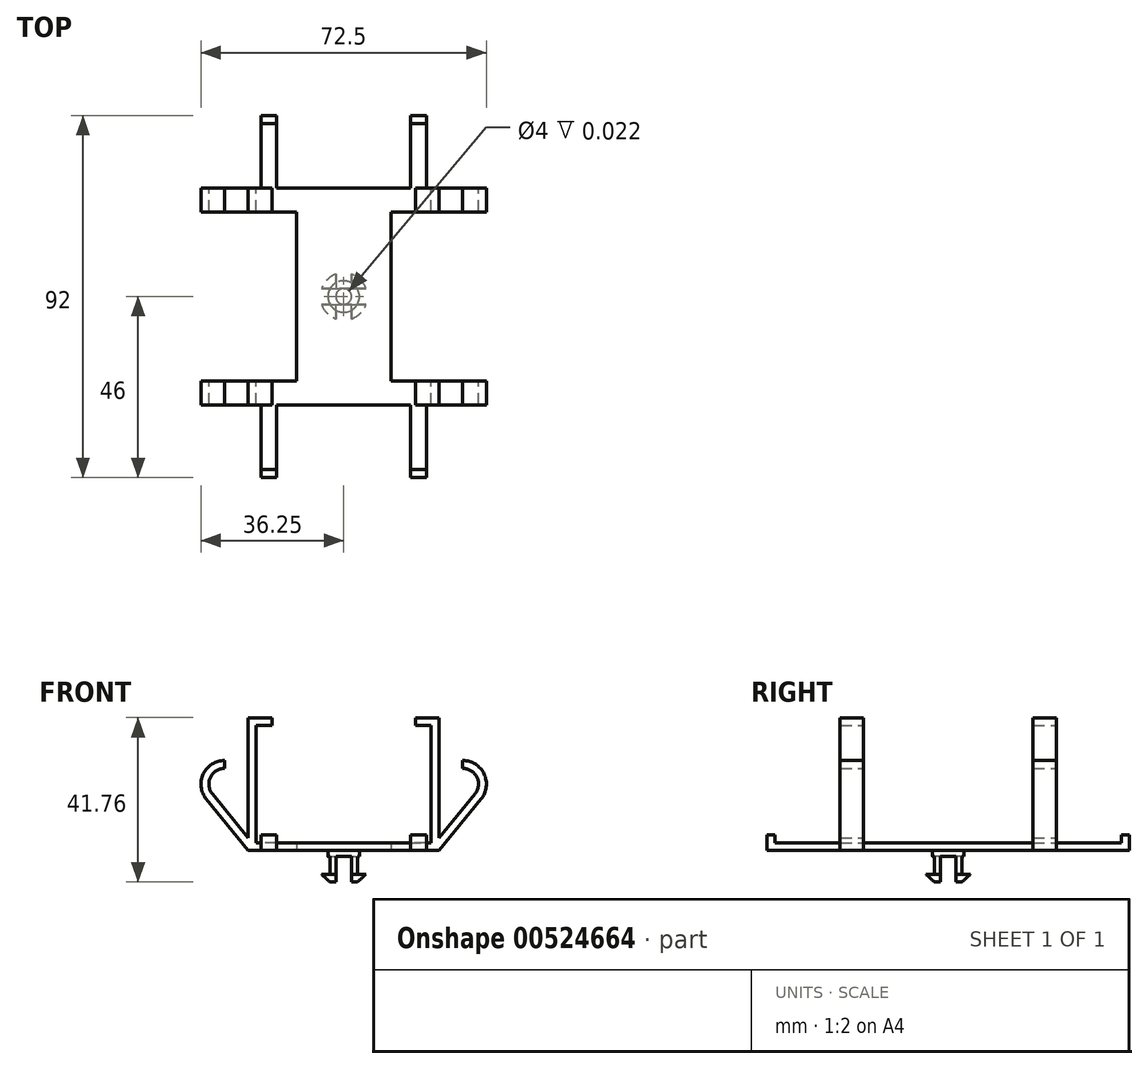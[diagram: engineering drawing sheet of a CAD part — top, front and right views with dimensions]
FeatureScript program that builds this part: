
annotation { "Feature Type Name" : "Feature", "Feature Type Description" : "" }
export const myFeature = defineFeature(function(context is Context, id is Id, definition is map)
    precondition{}
    {
        {
            var Q0;
            Q0=qCreatedBy(makeId("Front.planeOp"),FACE);
            var sketch = newSketch(context, id + "F0", { "sketchPlane" : qUnion([Q0])});
            skLineSegment(sketch, "E0.bottom", {"start": v(-22.25, 14.88) * mm, "end": v(22.25, 14.88) * mm});
            skLineSegment(sketch, "E0.top", {"start": v(-22.25, -14.88) * mm, "end": v(22.25, -14.88) * mm});
            skLineSegment(sketch, "E0.left", {"start": v(-22.25, 14.88) * mm, "end": v(-22.25, -14.88) * mm});
            skLineSegment(sketch, "E0.right", {"start": v(22.25, 14.88) * mm, "end": v(22.25, -14.88) * mm});
            skPoint(sketch, "E0.middle", {"position": v(0, 0) * mm});
            skLineSegment(sketch, "E1.bottom", {"start": v(24.25, 16.88) * mm, "end": v(18.25, 16.88) * mm});
            skLineSegment(sketch, "E1.top", {"start": v(24.25, -16.88) * mm, "end": v(4, -16.88) * mm});
            skLineSegment(sketch, "E1.left", {"start": v(24.25, 16.88) * mm, "end": v(24.25, -16.88) * mm});
            skLineSegment(sketch, "E1.right", {"start": v(-24.25, 16.88) * mm, "end": v(-24.25, -16.88) * mm});
            skLineSegment(sketch, "E2", {"start": v(-18.25, 16.88) * mm, "end": v(-18.25, 14.88) * mm});
            skLineSegment(sketch, "E3", {"start": v(18.25, 16.88) * mm, "end": v(18.25, 14.88) * mm});
            skLineSegment(sketch, "E4.trimOffspring", {"start": v(-18.25, 16.88) * mm, "end": v(-24.25, 16.88) * mm});
            skLineSegment(sketch, "E5.top", {"start": v(2, -24.88) * mm, "end": v(4, -24.88) * mm});
            skLineSegment(sketch, "E5.left", {"start": v(2, -18.35) * mm, "end": v(2, -24.88) * mm});
            skLineSegment(sketch, "E5.right", {"start": v(4, -16.88) * mm, "end": v(4, -22.88) * mm});
            skLineSegment(sketch, "E6", {"start": v(4, -24.88) * mm, "end": v(6, -22.88) * mm});
            skLineSegment(sketch, "E7", {"start": v(6, -22.88) * mm, "end": v(4, -22.88) * mm});
            skLineSegment(sketch, "E8.trimOffspring", {"start": v(2, -16.88) * mm, "end": v(-24.25, -16.87) * mm});
            skLineSegment(sketch, "E9", {"start": v(4, -16.88) * mm, "end": v(2, -16.88) * mm});
            skLineSegment(sketch, "E10", {"start": v(2, -18.35) * mm, "end": v(0, -18.35) * mm});
            skLineSegment(sketch, "E11", {"start": v(0, -18.35) * mm, "end": v(0, -16.88) * mm});
            skSolve(sketch);
        }
        {
            var Q0;
            Q0=makeQuery(id+"F0.imprint","IMPRINT",FACE,{"disambiguationData":[TD([[makeQuery(id+"F0.imprint","IMPRINT",EDGE,{"derivedFrom":sQuery(id+"F0.wireOp",EDGE,"E5.top")}),1.0]])]});
            var Q1;
            Q1=sQuery(id+"F0.wireOp",EDGE,"E11");
            revolve(context, id + "F1", {"entities" : qUnion([Q0]), "axis" : qUnion([Q1]), "revolveType" : RevolveType.FULL});
        }
        {
            var Q0;
            Q0=qCreatedBy(makeId("Front.planeOp"),FACE);
            var sketch = newSketch(context, id + "F2", { "sketchPlane" : qUnion([Q0])});
            skArc(sketch, "E12", {"start": v(33.35, -2.53) * mm, "mid": v(33.86, 1.72) * mm, "end": v(30.25, 4) * mm});
            skArc(sketch, "E13", {"start": v(34.9, -3.79) * mm, "mid": v(35.67, 2.58) * mm, "end": v(30.25, 6) * mm});
            skLineSegment(sketch, "E14", {"start": v(34.9, -3.79) * mm, "end": v(24.25, -16.88) * mm});
            skLineSegment(sketch, "E15", {"start": v(24.25, -16.88) * mm, "end": v(24.25, -13.7) * mm});
            skLineSegment(sketch, "E16.0", {"start": v(33.35, -2.53) * mm, "end": v(24.25, -13.7) * mm});
            skLineSegment(sketch, "E17", {"start": v(30.25, 4) * mm, "end": v(30.25, 6) * mm});
            skArc(sketch, "E18.MirrorCS", {"start": v(-34.9, -3.79) * mm, "mid": v(-35.67, 2.58) * mm, "end": v(-30.25, 6) * mm});
            skLineSegment(sketch, "E19.MirrorCS", {"start": v(-33.35, -2.53) * mm, "end": v(-24.25, -13.7) * mm});
            skArc(sketch, "E20.MirrorCS", {"start": v(-33.35, -2.53) * mm, "mid": v(-33.86, 1.72) * mm, "end": v(-30.25, 4) * mm});
            skLineSegment(sketch, "E21.MirrorCS", {"start": v(-30.25, 4) * mm, "end": v(-30.25, 6) * mm});
            skLineSegment(sketch, "E22.MirrorCS", {"start": v(-24.25, -16.88) * mm, "end": v(-24.25, -13.7) * mm});
            skLineSegment(sketch, "E23.MirrorCS", {"start": v(-34.9, -3.79) * mm, "end": v(-24.25, -16.88) * mm});
            skSolve(sketch);
        }
        {
            var Q0;
            Q0=makeQuery(id+"F0.imprint","IMPRINT",FACE,{"disambiguationData":[TD([[makeQuery(id+"F0.imprint","IMPRINT",EDGE,{"derivedFrom":sQuery(id+"F0.wireOp",EDGE,"E0.top")}),-1.0]])]});
            extrude(context, id + "F3", {"entities" : qUnion([Q0]), "operationType" : NewBodyOperationType.ADD, "endBound" : BoundingType.SYMMETRIC, "depth" : 55 * mm, "offsetDistance" : 25 * mm});
        }
        {
            var Q0;
            Q0=makeQuery(id+"F3.opExtrude","SWEPT_FACE",FACE,{"disambiguationData":[OSD([sQuery(id+"F0.wireOp",EDGE,"E1.top"),sQuery(id+"F0.wireOp",EDGE,"E8.trimOffspring"),sQuery(id+"F0.wireOp",EDGE,"E9")])]});
            var sketch = newSketch(context, id + "F4", { "sketchPlane" : qUnion([Q0])});
            skPoint(sketch, "E24.start.orphan", {"position": v(-24.25, 20) * mm});
            skPoint(sketch, "E25.end.orphan", {"position": v(-18.25, 0) * mm});
            skPoint(sketch, "E25.start.orphan", {"position": v(-18.25, 20) * mm});
            skPoint(sketch, "E26.MirrorCS.end.orphan", {"position": v(-18.25, -20) * mm});
            skPoint(sketch, "E26.MirrorCS.start.orphan", {"position": v(-24.25, -20) * mm});
            skPoint(sketch, "E27.MirrorCS.start.orphan", {"position": v(24.25, 20) * mm});
            skPoint(sketch, "E28.MirrorCS.end.orphan", {"position": v(18.25, 0) * mm});
            skPoint(sketch, "E28.MirrorCS.start.orphan", {"position": v(18.25, 20) * mm});
            skPoint(sketch, "E29.MirrorCS.end.orphan", {"position": v(18.25, -20) * mm});
            skPoint(sketch, "E29.MirrorCS.start.orphan", {"position": v(24.25, -20) * mm});
            skLineSegment(sketch, "E30.bottom", {"start": v(-40, 21.5) * mm, "end": v(-12, 21.5) * mm});
            skLineSegment(sketch, "E30.top", {"start": v(-40, -21.5) * mm, "end": v(-12, -21.5) * mm});
            skLineSegment(sketch, "E30.left", {"start": v(-40, 21.5) * mm, "end": v(-40, -21.5) * mm});
            skLineSegment(sketch, "E30.right", {"start": v(-12, 21.5) * mm, "end": v(-12, -21.5) * mm});
            skPoint(sketch, "E30.middle", {"position": v(-26, 0) * mm});
            skLineSegment(sketch, "E31.MirrorCS", {"start": v(40, -21.5) * mm, "end": v(12, -21.5) * mm});
            skLineSegment(sketch, "E32.MirrorCS", {"start": v(40, 21.5) * mm, "end": v(40, -21.5) * mm});
            skPoint(sketch, "E33.MirrorP", {"position": v(26, 0) * mm});
            skLineSegment(sketch, "E34.MirrorCS", {"start": v(12, 21.5) * mm, "end": v(12, -21.5) * mm});
            skLineSegment(sketch, "E35.MirrorCS", {"start": v(40, 21.5) * mm, "end": v(12, 21.5) * mm});
            skSolve(sketch);
        }
        {
            var Q0;
            Q0 = qSketchRegion(id + "F2", true);
            extrude(context, id + "F5", {"entities" : qUnion([Q0]), "operationType" : NewBodyOperationType.ADD, "endBound" : BoundingType.SYMMETRIC, "depth" : 55 * mm, "offsetDistance" : 25 * mm});
        }
        {
            var Q0;
            {var subQ0=sQuery(id+"F4.wireOp",EDGE,"E30.left");Q0=makeQuery(id+"F4.imprint","IMPRINT",FACE,{"disambiguationData":[TD([[makeQuery(id+"F4.imprint","IMPRINT",EDGE,{"derivedFrom":subQ0}),1.0]])]});}
            var Q1;
            {var subQ0=sQuery(id+"F4.wireOp",EDGE,"E30.right");Q1=makeQuery(id+"F4.imprint","IMPRINT",FACE,{"disambiguationData":[TD([[makeQuery(id+"F4.imprint","IMPRINT",EDGE,{"derivedFrom":subQ0}),-1.0]])]});}
            var Q2;
            {var subQ0=sQuery(id+"F4.wireOp",EDGE,"E34.MirrorCS");Q2=makeQuery(id+"F4.imprint","IMPRINT",FACE,{"disambiguationData":[TD([[makeQuery(id+"F4.imprint","IMPRINT",EDGE,{"derivedFrom":subQ0}),1.0]])]});}
            var Q3;
            {var subQ0=sQuery(id+"F4.wireOp",EDGE,"E32.MirrorCS");Q3=makeQuery(id+"F4.imprint","IMPRINT",FACE,{"disambiguationData":[TD([[makeQuery(id+"F4.imprint","IMPRINT",EDGE,{"derivedFrom":subQ0}),-1.0]])]});}
            extrude(context, id + "F6", {"entities" : qUnion([Q0, Q1, Q2, Q3]), "operationType" : NewBodyOperationType.REMOVE, "endBound" : BoundingType.THROUGH_ALL, "oppositeDirection" : true, "depth" : 25 * mm, "offsetDistance" : 25 * mm});
        }
        {
            var Q0;
            Q0=qCreatedBy(makeId("Right.planeOp"),FACE);
            var sketch = newSketch(context, id + "F7", { "sketchPlane" : qUnion([Q0])});
            skLineSegment(sketch, "E36", {"start": v(-27.5, -16.88) * mm, "end": v(-46, -16.88) * mm});
            skLineSegment(sketch, "E37", {"start": v(-46, -16.88) * mm, "end": v(-46, -12.88) * mm});
            skLineSegment(sketch, "E38", {"start": v(-46, -12.88) * mm, "end": v(-44, -12.88) * mm});
            skLineSegment(sketch, "E39", {"start": v(-44, -12.88) * mm, "end": v(-44, -14.88) * mm});
            skLineSegment(sketch, "E40", {"start": v(-44, -14.88) * mm, "end": v(-27.5, -14.88) * mm});
            skLineSegment(sketch, "E41.MirrorCS", {"start": v(46, -12.88) * mm, "end": v(44, -12.88) * mm});
            skLineSegment(sketch, "E42.MirrorCS", {"start": v(44, -12.88) * mm, "end": v(44, -14.88) * mm});
            skLineSegment(sketch, "E43.MirrorCS", {"start": v(27.5, -16.88) * mm, "end": v(46, -16.88) * mm});
            skLineSegment(sketch, "E44.MirrorCS", {"start": v(46, -16.88) * mm, "end": v(46, -12.88) * mm});
            skLineSegment(sketch, "E45.MirrorCS", {"start": v(44, -14.88) * mm, "end": v(27.5, -14.88) * mm});
            skLineSegment(sketch, "E46", {"start": v(-27.5, -14.87) * mm, "end": v(-27.5, -16.88) * mm});
            skLineSegment(sketch, "E47", {"start": v(27.5, -14.87) * mm, "end": v(27.5, -16.88) * mm});
            skSolve(sketch);
        }
        {
            var Q0;
            Q0 = qSketchRegion(id + "F7", true);
            extrude(context, id + "F8", {"entities" : qUnion([Q0]), "operationType" : NewBodyOperationType.ADD, "endBound" : BoundingType.SYMMETRIC, "depth" : 42 * mm, "offsetDistance" : 25 * mm});
        }
        {
            var Q0;
            Q0=makeQuery(id+"F8.boolean.opBoolean","MERGE",FACE,{"derivedFrom":[makeQuery(id+"F3.opExtrude","SWEPT_FACE",FACE,{"disambiguationData":[OSD([sQuery(id+"F0.wireOp",EDGE,"E1.top"),sQuery(id+"F0.wireOp",EDGE,"E8.trimOffspring"),sQuery(id+"F0.wireOp",EDGE,"E9")])]}),makeQuery(id+"F8.opExtrude","SWEPT_FACE",FACE,{"disambiguationData":[OSD([sQuery(id+"F7.wireOp",EDGE,"E36")])]}),makeQuery(id+"F8.opExtrude","SWEPT_FACE",FACE,{"disambiguationData":[OSD([sQuery(id+"F7.wireOp",EDGE,"E43.MirrorCS")])]})]});
            var sketch = newSketch(context, id + "F9", { "sketchPlane" : qUnion([Q0])});
            skLineSegment(sketch, "E48", {"start": v(-17, 46) * mm, "end": v(-17, 27.5) * mm});
            skLineSegment(sketch, "E49", {"start": v(-17, 27.5) * mm, "end": v(0, 27.5) * mm});
            skPoint(sketch, "E50.orphan", {"position": v(-17, 20) * mm});
            skLineSegment(sketch, "E51.MirrorCS", {"start": v(17, 46) * mm, "end": v(17, 27.5) * mm});
            skLineSegment(sketch, "E52.MirrorCS", {"start": v(17, 27.5) * mm, "end": v(0, 27.5) * mm});
            skLineSegment(sketch, "E53.MirrorCS", {"start": v(17, -46) * mm, "end": v(17, -27.5) * mm});
            skLineSegment(sketch, "E54.MirrorCS", {"start": v(-17, -46) * mm, "end": v(-17, -27.5) * mm});
            skLineSegment(sketch, "E55.MirrorCS", {"start": v(17, -27.5) * mm, "end": v(0, -27.5) * mm});
            skLineSegment(sketch, "E56.MirrorCS", {"start": v(-17, -27.5) * mm, "end": v(0, -27.5) * mm});
            skSolve(sketch);
        }
        {
            var Q0;
            {var subQ1=sQuery(id+"F9.wireOp",EDGE,"E48");Q0=makeQuery(id+"F9.imprint","IMPRINT",FACE,{"disambiguationData":[TD([[makeQuery(id+"F9.imprint","IMPRINT",EDGE,{"derivedFrom":subQ1}),1.0]])]});}
            var Q1;
            {var subQ1=sQuery(id+"F9.wireOp",EDGE,"E54.MirrorCS");Q1=makeQuery(id+"F9.imprint","IMPRINT",FACE,{"disambiguationData":[TD([[makeQuery(id+"F9.imprint","IMPRINT",EDGE,{"derivedFrom":subQ1}),-1.0]])]});}
            extrude(context, id + "F10", {"entities" : qUnion([Q0, Q1]), "operationType" : NewBodyOperationType.REMOVE, "endBound" : BoundingType.THROUGH_ALL, "oppositeDirection" : true, "depth" : 25 * mm, "offsetDistance" : 25 * mm});
        }
        {
            var Q0;
            Q0=qCreatedBy(makeId("Front.planeOp"),FACE);
            var sketch = newSketch(context, id + "F11", { "sketchPlane" : qUnion([Q0])});
            skLineSegment(sketch, "E57.bottom", {"start": v(0, -18.4) * mm, "end": v(2, -18.4) * mm});
            skLineSegment(sketch, "E57.top", {"start": v(0, -24.9) * mm, "end": v(2, -24.9) * mm});
            skLineSegment(sketch, "E57.left", {"start": v(0, -18.4) * mm, "end": v(0, -24.9) * mm});
            skLineSegment(sketch, "E57.right", {"start": v(2, -18.4) * mm, "end": v(2, -24.9) * mm});
            skLineSegment(sketch, "E58.MirrorCS", {"start": v(-2, -18.4) * mm, "end": v(-2, -24.9) * mm});
            skLineSegment(sketch, "E59.MirrorCS", {"start": v(0, -24.9) * mm, "end": v(-2, -24.9) * mm});
            skLineSegment(sketch, "E60.MirrorCS", {"start": v(0, -18.4) * mm, "end": v(-2, -18.4) * mm});
            skSolve(sketch);
        }
        {
            var Q0;
            Q0 = qSketchRegion(id + "F11", true);
            extrude(context, id + "F12", {"entities" : qUnion([Q0]), "operationType" : NewBodyOperationType.REMOVE, "endBound" : BoundingType.SYMMETRIC, "oppositeDirection" : true, "depth" : 20 * mm, "offsetDistance" : 25 * mm});
        }
        {
            var Q0;
            Q0=qCreatedBy(makeId("Right.planeOp"),FACE);
            var sketch = newSketch(context, id + "F13", { "sketchPlane" : qUnion([Q0])});
            skLineSegment(sketch, "E61.bottom", {"start": v(0, -18.38) * mm, "end": v(2, -18.38) * mm});
            skLineSegment(sketch, "E61.top", {"start": v(0, -24.88) * mm, "end": v(2, -24.88) * mm});
            skLineSegment(sketch, "E61.left", {"start": v(0, -18.38) * mm, "end": v(0, -24.88) * mm});
            skLineSegment(sketch, "E61.right", {"start": v(2, -18.38) * mm, "end": v(2, -24.88) * mm});
            skLineSegment(sketch, "E62.MirrorCS", {"start": v(0, -18.38) * mm, "end": v(-2, -18.38) * mm});
            skLineSegment(sketch, "E63.MirrorCS", {"start": v(0, -24.88) * mm, "end": v(-2, -24.88) * mm});
            skLineSegment(sketch, "E64.MirrorCS", {"start": v(-2, -18.38) * mm, "end": v(-2, -24.88) * mm});
            skSolve(sketch);
        }
        {
            var Q0;
            Q0 = qSketchRegion(id + "F13", true);
            extrude(context, id + "F14", {"entities" : qUnion([Q0]), "operationType" : NewBodyOperationType.REMOVE, "endBound" : BoundingType.SYMMETRIC, "oppositeDirection" : true, "depth" : 25 * mm, "offsetDistance" : 25 * mm});
        }
    });
